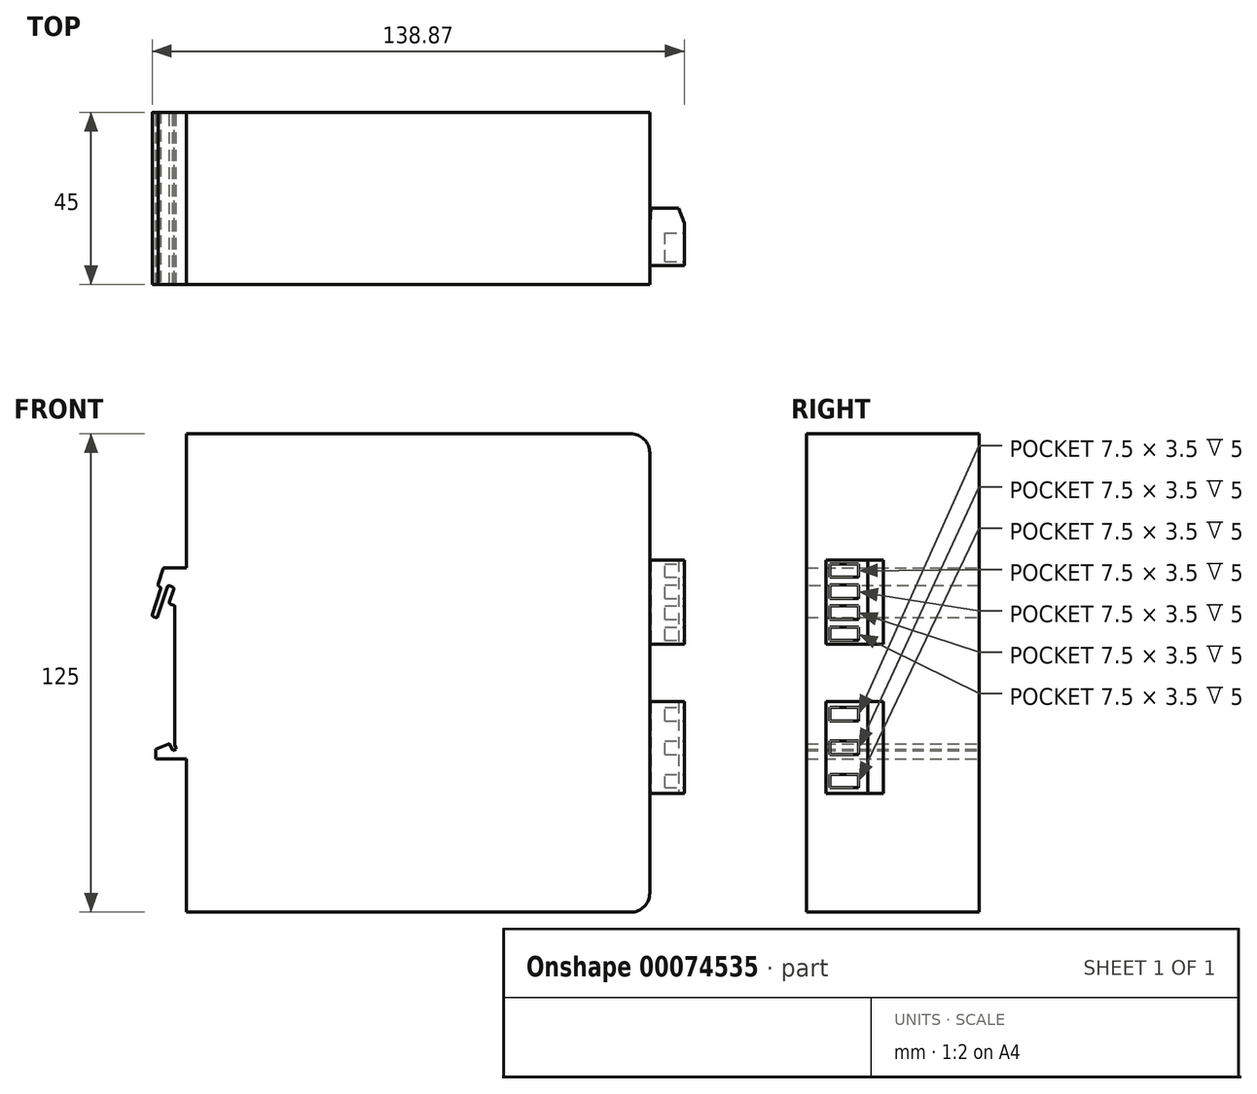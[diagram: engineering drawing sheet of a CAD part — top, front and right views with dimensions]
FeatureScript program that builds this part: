
annotation { "Feature Type Name" : "Feature", "Feature Type Description" : "" }
export const myFeature = defineFeature(function(context is Context, id is Id, definition is map)
    precondition{}
    {
        {
            var Q0;
            Q0=qCreatedBy(makeId("Top.planeOp"),FACE);
            var sketch = newSketch(context, id + "F0", { "sketchPlane" : qUnion([Q0])});
            skLineSegment(sketch, "E0.bottom", {"start": v(-60.5, 22.5) * mm, "end": v(60.5, 22.5) * mm});
            skLineSegment(sketch, "E0.top", {"start": v(-60.5, -22.5) * mm, "end": v(60.5, -22.5) * mm});
            skLineSegment(sketch, "E0.left", {"start": v(-60.5, 22.5) * mm, "end": v(-60.5, -22.5) * mm});
            skLineSegment(sketch, "E0.right", {"start": v(60.5, 22.5) * mm, "end": v(60.5, -22.5) * mm});
            skLineSegment(sketch, "E1", {"start": v(-60.5, 22.5) * mm, "end": v(60.5, -22.5) * mm, "construction": true});
            skLineSegment(sketch, "E2", {"start": v(-60.5, -22.5) * mm, "end": v(60.5, 22.5) * mm, "construction": true});
            skPoint(sketch, "E3", {"position": v(0, 0) * mm});
            skPoint(sketch, "E3.positionSnap0", {"position": v(0, 0) * mm});
            skSolve(sketch);
        }
        {
            var Q0;
            Q0=makeQuery(id+"F0.imprint","IMPRINT",FACE,{"disambiguationData":[TD([[makeQuery(id+"F0.imprint","IMPRINT",EDGE,{"derivedFrom":sQuery(id+"F0.wireOp",EDGE,"E0.bottom")}),-1.0]])]});
            extrude(context, id + "F1", {"entities" : qUnion([Q0]), "depth" : 125 * mm});
        }
        {
            var Q0;
            Q0=makeQuery(id+"F1.opExtrude","CAP_EDGE",EDGE,{"disambiguationData":[OSD([sQuery(id+"F0.wireOp",EDGE,"E0.right")])],"isStart":false});
            var Q1;
            Q1=makeQuery(id+"F1.opExtrude","CAP_EDGE",EDGE,{"disambiguationData":[OSD([sQuery(id+"F0.wireOp",EDGE,"E0.right")])],"isStart":true});
            fillet(context, id + "F2", {"entities" : qUnion([Q0, Q1]), "radius" : 5 * mm, "tangentPropagation" : true, "allowEdgeOverflow" : false});
        }
        {
            var Q0;
            Q0=makeQuery(id+"F1.opExtrude","SWEPT_FACE",FACE,{"disambiguationData":[OSD([sQuery(id+"F0.wireOp",EDGE,"E0.right")])]});
            var sketch = newSketch(context, id + "F3", { "sketchPlane" : qUnion([Q0])});
            skLineSegment(sketch, "E4.bottom", {"start": v(-17.5, 92) * mm, "end": v(-6.5, 92) * mm});
            skLineSegment(sketch, "E4.top", {"start": v(-17.5, 70) * mm, "end": v(-6.5, 70) * mm});
            skLineSegment(sketch, "E4.left", {"start": v(-17.5, 92) * mm, "end": v(-17.5, 70) * mm});
            skLineSegment(sketch, "E4.right", {"start": v(-6.5, 92) * mm, "end": v(-6.5, 70) * mm});
            skLineSegment(sketch, "E5.bottom", {"start": v(-17.5, 55) * mm, "end": v(-6.5, 55) * mm});
            skLineSegment(sketch, "E5.top", {"start": v(-17.5, 31) * mm, "end": v(-6.5, 31) * mm});
            skLineSegment(sketch, "E5.left", {"start": v(-17.5, 55) * mm, "end": v(-17.5, 31) * mm});
            skLineSegment(sketch, "E5.right", {"start": v(-6.5, 55) * mm, "end": v(-6.5, 31) * mm});
            skSolve(sketch);
        }
        {
            var Q0;
            Q0=makeQuery(id+"F3.imprint","IMPRINT",FACE,{"disambiguationData":[TD([[makeQuery(id+"F3.imprint","IMPRINT",EDGE,{"derivedFrom":sQuery(id+"F3.wireOp",EDGE,"E4.bottom")}),-1.0]])]});
            var Q1;
            Q1=makeQuery(id+"F3.imprint","IMPRINT",FACE,{"disambiguationData":[TD([[makeQuery(id+"F3.imprint","IMPRINT",EDGE,{"derivedFrom":sQuery(id+"F3.wireOp",EDGE,"E5.bottom")}),-1.0]])]});
            extrude(context, id + "F4", {"entities" : qUnion([Q0, Q1]), "depth" : 9 * mm});
        }
        {
            var Q0;
            Q0=makeQuery(id+"F4.opExtrude","SWEPT_FACE",FACE,{"disambiguationData":[OSD([sQuery(id+"F3.wireOp",EDGE,"E4.top")])]});
            var sketch = newSketch(context, id + "F5", { "sketchPlane" : qUnion([Q0])});
            skLineSegment(sketch, "E6", {"start": v(69.5, 6.5) * mm, "end": v(68.04, 2.5) * mm});
            skLineSegment(sketch, "E7", {"start": v(68.04, 2.5) * mm, "end": v(60.85, 2.5) * mm});
            skLineSegment(sketch, "E8", {"start": v(60.85, 2.5) * mm, "end": v(60.5, 6.5) * mm});
            skLineSegment(sketch, "E9", {"start": v(60.5, 6.5) * mm, "end": v(69.5, 6.5) * mm});
            skLineSegment(sketch, "E10", {"start": v(68.39, 3.44) * mm, "end": v(68.04, 2.5) * mm});
            skLineSegment(sketch, "E11", {"start": v(68.04, 2.5) * mm, "end": v(69.04, 2.5) * mm});
            skLineSegment(sketch, "E12", {"start": v(69.04, 2.5) * mm, "end": v(68.39, 3.44) * mm});
            skSolve(sketch);
        }
        {
            var Q0;
            Q0=makeQuery(id+"F5.imprint","IMPRINT",FACE,{"disambiguationData":[TD([[makeQuery(id+"F5.imprint","IMPRINT",EDGE,{"derivedFrom":sQuery(id+"F5.wireOp",EDGE,"E6")}),-1.0]])]});
            var Q1;
            Q1=makeQuery(id+"F5.imprint","IMPRINT",FACE,{"disambiguationData":[TD([[makeQuery(id+"F5.imprint","IMPRINT",EDGE,{"derivedFrom":sQuery(id+"F5.wireOp",EDGE,"E10")}),1.0]])]});
            var Q2;
            Q2=makeQuery(id+"F4.opExtrude","SWEPT_FACE",FACE,{"disambiguationData":[OSD([sQuery(id+"F3.wireOp",EDGE,"E4.bottom")])]});
            extrude(context, id + "F6", {"entities" : qUnion([Q0, Q1]), "operationType" : NewBodyOperationType.ADD, "endBound" : BoundingType.UP_TO_SURFACE, "oppositeDirection" : true, "endBoundEntityFace" : qUnion([Q2]), "depth" : 25 * mm});
        }
        {
            var Q0;
            Q0=makeQuery(id+"F4.opExtrude","SWEPT_FACE",FACE,{"disambiguationData":[OSD([sQuery(id+"F3.wireOp",EDGE,"E5.top")])]});
            var sketch = newSketch(context, id + "F7", { "sketchPlane" : qUnion([Q0])});
            skLineSegment(sketch, "E13", {"start": v(69.5, 6.5) * mm, "end": v(68.04, 2.5) * mm});
            skLineSegment(sketch, "E14", {"start": v(68.04, 2.5) * mm, "end": v(60.85, 2.5) * mm});
            skLineSegment(sketch, "E15", {"start": v(60.85, 2.5) * mm, "end": v(60.5, 6.5) * mm});
            skLineSegment(sketch, "E16", {"start": v(60.5, 6.5) * mm, "end": v(69.5, 6.5) * mm});
            skLineSegment(sketch, "E17", {"start": v(68.39, 3.44) * mm, "end": v(68.04, 2.5) * mm});
            skLineSegment(sketch, "E18", {"start": v(68.04, 2.5) * mm, "end": v(69.04, 2.5) * mm});
            skLineSegment(sketch, "E19", {"start": v(69.04, 2.5) * mm, "end": v(68.39, 3.44) * mm});
            skSolve(sketch);
        }
        {
            var Q0;
            Q0=makeQuery(id+"F7.imprint","IMPRINT",FACE,{"disambiguationData":[TD([[makeQuery(id+"F7.imprint","IMPRINT",EDGE,{"derivedFrom":sQuery(id+"F7.wireOp",EDGE,"E13")}),-1.0]])]});
            var Q1;
            Q1=makeQuery(id+"F7.imprint","IMPRINT",FACE,{"disambiguationData":[TD([[makeQuery(id+"F7.imprint","IMPRINT",EDGE,{"derivedFrom":sQuery(id+"F7.wireOp",EDGE,"E17")}),1.0]])]});
            var Q2;
            Q2=makeQuery(id+"F4.opExtrude","SWEPT_FACE",FACE,{"disambiguationData":[OSD([sQuery(id+"F3.wireOp",EDGE,"E5.bottom")])]});
            extrude(context, id + "F8", {"entities" : qUnion([Q0, Q1]), "operationType" : NewBodyOperationType.ADD, "endBound" : BoundingType.UP_TO_SURFACE, "oppositeDirection" : true, "endBoundEntityFace" : qUnion([Q2]), "depth" : 25 * mm});
        }
        {
            var Q0;
            Q0=makeQuery(id+"F4.opExtrude","CAP_FACE",FACE,{"disambiguationData":[OSD([sQuery(id+"F3.wireOp",EDGE,"E5.bottom"),sQuery(id+"F3.wireOp",EDGE,"E5.top"),sQuery(id+"F3.wireOp",EDGE,"E5.left"),sQuery(id+"F3.wireOp",EDGE,"E5.right")])],"isStart":false});
            var sketch = newSketch(context, id + "F9", { "sketchPlane" : qUnion([Q0])});
            skLineSegment(sketch, "E20.bottom", {"start": v(-16.5, 32.5) * mm, "end": v(-9, 32.5) * mm});
            skLineSegment(sketch, "E20.top", {"start": v(-16.5, 36) * mm, "end": v(-9, 36) * mm});
            skLineSegment(sketch, "E20.left", {"start": v(-16.5, 32.5) * mm, "end": v(-16.5, 36) * mm});
            skLineSegment(sketch, "E20.right", {"start": v(-9, 32.5) * mm, "end": v(-9, 36) * mm});
            skLineSegment(sketch, "E21.bottom", {"start": v(-16.5, 41.25) * mm, "end": v(-9, 41.25) * mm});
            skLineSegment(sketch, "E21.top", {"start": v(-16.5, 44.75) * mm, "end": v(-9, 44.75) * mm});
            skLineSegment(sketch, "E21.left", {"start": v(-16.5, 41.25) * mm, "end": v(-16.5, 44.75) * mm});
            skLineSegment(sketch, "E21.right", {"start": v(-9, 41.25) * mm, "end": v(-9, 44.75) * mm});
            skLineSegment(sketch, "E22.bottom", {"start": v(-16.5, 50) * mm, "end": v(-9, 50) * mm});
            skLineSegment(sketch, "E22.top", {"start": v(-16.5, 53.5) * mm, "end": v(-9, 53.5) * mm});
            skLineSegment(sketch, "E22.left", {"start": v(-16.5, 50) * mm, "end": v(-16.5, 53.5) * mm});
            skLineSegment(sketch, "E22.right", {"start": v(-9, 50) * mm, "end": v(-9, 53.5) * mm});
            skLineSegment(sketch, "E23.bottom", {"start": v(-16.5, 71) * mm, "end": v(-9, 71) * mm});
            skLineSegment(sketch, "E23.top", {"start": v(-16.5, 74.5) * mm, "end": v(-9, 74.5) * mm});
            skLineSegment(sketch, "E23.left", {"start": v(-16.5, 71) * mm, "end": v(-16.5, 74.5) * mm});
            skLineSegment(sketch, "E23.right", {"start": v(-9, 71) * mm, "end": v(-9, 74.5) * mm});
            skLineSegment(sketch, "E24.bottom", {"start": v(-16.5, 76.5) * mm, "end": v(-9, 76.5) * mm});
            skLineSegment(sketch, "E24.top", {"start": v(-16.5, 80) * mm, "end": v(-9, 80) * mm});
            skLineSegment(sketch, "E24.left", {"start": v(-16.5, 76.5) * mm, "end": v(-16.5, 80) * mm});
            skLineSegment(sketch, "E24.right", {"start": v(-9, 76.5) * mm, "end": v(-9, 80) * mm});
            skLineSegment(sketch, "E25.bottom", {"start": v(-16.5, 82) * mm, "end": v(-9, 82) * mm});
            skLineSegment(sketch, "E25.top", {"start": v(-16.5, 85.5) * mm, "end": v(-9, 85.5) * mm});
            skLineSegment(sketch, "E25.left", {"start": v(-16.5, 82) * mm, "end": v(-16.5, 85.5) * mm});
            skLineSegment(sketch, "E25.right", {"start": v(-9, 82) * mm, "end": v(-9, 85.5) * mm});
            skLineSegment(sketch, "E26.bottom", {"start": v(-16.5, 87.5) * mm, "end": v(-9, 87.5) * mm});
            skLineSegment(sketch, "E26.top", {"start": v(-16.5, 91) * mm, "end": v(-9, 91) * mm});
            skLineSegment(sketch, "E26.left", {"start": v(-16.5, 87.5) * mm, "end": v(-16.5, 91) * mm});
            skLineSegment(sketch, "E26.right", {"start": v(-9, 87.5) * mm, "end": v(-9, 91) * mm});
            skSolve(sketch);
        }
        {
            var Q0;
            Q0=makeQuery(id+"F9.imprint","IMPRINT",FACE,{"disambiguationData":[TD([[makeQuery(id+"F9.imprint","IMPRINT",EDGE,{"derivedFrom":sQuery(id+"F9.wireOp",EDGE,"E20.bottom")}),1.0]])]});
            var Q1;
            Q1=makeQuery(id+"F9.imprint","IMPRINT",FACE,{"disambiguationData":[TD([[makeQuery(id+"F9.imprint","IMPRINT",EDGE,{"derivedFrom":sQuery(id+"F9.wireOp",EDGE,"tqbWb7Cq-eTrh-Zdbz-2FrB-U6ubUCRYbAbA.bottom")}),1.0]])]});
            var Q2;
            Q2=makeQuery(id+"F9.imprint","IMPRINT",FACE,{"disambiguationData":[TD([[makeQuery(id+"F9.imprint","IMPRINT",EDGE,{"derivedFrom":sQuery(id+"F9.wireOp",EDGE,"E21.bottom")}),1.0]])]});
            var Q3;
            Q3=makeQuery(id+"F9.imprint","IMPRINT",FACE,{"disambiguationData":[TD([[makeQuery(id+"F9.imprint","IMPRINT",EDGE,{"derivedFrom":sQuery(id+"F9.wireOp",EDGE,"E22.bottom")}),1.0]])]});
            extrude(context, id + "F10", {"entities" : qUnion([Q0, Q1, Q2, Q3]), "operationType" : NewBodyOperationType.REMOVE, "oppositeDirection" : true, "depth" : 5 * mm});
        }
        {
            var Q0;
            Q0=makeQuery(id+"F9.imprint","IMPRINT",FACE,{"disambiguationData":[TD([[makeQuery(id+"F9.imprint","IMPRINT",EDGE,{"derivedFrom":sQuery(id+"F9.wireOp",EDGE,"E23.bottom")}),1.0]])]});
            var Q1;
            Q1=makeQuery(id+"F9.imprint","IMPRINT",FACE,{"disambiguationData":[TD([[makeQuery(id+"F9.imprint","IMPRINT",EDGE,{"derivedFrom":sQuery(id+"F9.wireOp",EDGE,"E24.bottom")}),1.0]])]});
            var Q2;
            Q2=makeQuery(id+"F9.imprint","IMPRINT",FACE,{"disambiguationData":[TD([[makeQuery(id+"F9.imprint","IMPRINT",EDGE,{"derivedFrom":sQuery(id+"F9.wireOp",EDGE,"E25.bottom")}),1.0]])]});
            var Q3;
            Q3=makeQuery(id+"F9.imprint","IMPRINT",FACE,{"disambiguationData":[TD([[makeQuery(id+"F9.imprint","IMPRINT",EDGE,{"derivedFrom":sQuery(id+"F9.wireOp",EDGE,"E26.bottom")}),1.0]])]});
            extrude(context, id + "F11", {"entities" : qUnion([Q0, Q1, Q2, Q3]), "operationType" : NewBodyOperationType.REMOVE, "oppositeDirection" : true, "depth" : 5 * mm});
        }
        {
            var Q0;
            Q0=makeQuery(id+"F1.opExtrude","SWEPT_FACE",FACE,{"disambiguationData":[OSD([sQuery(id+"F0.wireOp",EDGE,"E0.bottom")])]});
            var sketch = newSketch(context, id + "F12", { "sketchPlane" : qUnion([Q0])});
            skLineSegment(sketch, "E27", {"start": v(60.5, 40) * mm, "end": v(60.5, 90) * mm});
            skLineSegment(sketch, "E28", {"start": v(60.5, 90) * mm, "end": v(66.5, 90) * mm});
            skLineSegment(sketch, "E29", {"start": v(66.5, 90) * mm, "end": v(68.02, 85.24) * mm});
            skLineSegment(sketch, "E30", {"start": v(68.02, 85.24) * mm, "end": v(67.07, 84.93) * mm});
            skLineSegment(sketch, "E31", {"start": v(67.07, 84.93) * mm, "end": v(69.5, 77.31) * mm});
            skLineSegment(sketch, "E32", {"start": v(69.5, 77.31) * mm, "end": v(68.07, 76.86) * mm});
            skLineSegment(sketch, "E33", {"start": v(68.07, 76.86) * mm, "end": v(65.33, 85.43) * mm});
            skLineSegment(sketch, "E34", {"start": v(65.33, 85.43) * mm, "end": v(63.68, 84.9) * mm});
            skLineSegment(sketch, "E35", {"start": v(63.68, 84.9) * mm, "end": v(65.04, 80.61) * mm});
            skLineSegment(sketch, "E36", {"start": v(65.04, 80.61) * mm, "end": v(63.5, 80.12) * mm});
            skLineSegment(sketch, "E37", {"start": v(63.5, 80.12) * mm, "end": v(63.5, 43.55) * mm});
            skLineSegment(sketch, "E38", {"start": v(63.5, 43.55) * mm, "end": v(63.12, 42.62) * mm});
            skLineSegment(sketch, "E39", {"start": v(63.12, 42.62) * mm, "end": v(64.04, 42.24) * mm});
            skLineSegment(sketch, "E40", {"start": v(64.04, 42.24) * mm, "end": v(64.8, 44.09) * mm});
            skLineSegment(sketch, "E41", {"start": v(64.8, 44.09) * mm, "end": v(68.5, 42.55) * mm});
            skLineSegment(sketch, "E42", {"start": v(68.5, 42.55) * mm, "end": v(68.5, 40.05) * mm});
            skLineSegment(sketch, "E43", {"start": v(68.5, 40.05) * mm, "end": v(60.5, 40) * mm});
            skSolve(sketch);
        }
        {
            var Q0;
            Q0=makeQuery(id+"F12.imprint","IMPRINT",FACE,{"disambiguationData":[TD([[makeQuery(id+"F12.imprint","IMPRINT",EDGE,{"derivedFrom":sQuery(id+"F12.wireOp",EDGE,"E27")}),1.0]])]});
            var Q1;
            Q1=makeQuery(id+"F1.opExtrude","SWEPT_FACE",FACE,{"disambiguationData":[OSD([sQuery(id+"F0.wireOp",EDGE,"E0.top")])]});
            extrude(context, id + "F13", {"entities" : qUnion([Q0]), "operationType" : NewBodyOperationType.ADD, "endBound" : BoundingType.UP_TO_SURFACE, "oppositeDirection" : true, "endBoundEntityFace" : qUnion([Q1]), "depth" : 25 * mm});
        }
        {
            var Q0;
            Q0=makeQuery(id+"F13.opExtrude","SWEPT_EDGE",EDGE,{"disambiguationData":[OSD([sQuery(id+"F12.wireOp",EDGE,"E30"),sQuery(id+"F12.wireOp",EDGE,"E31")])]});
            var Q1;
            Q1=makeQuery(id+"F13.opExtrude","SWEPT_EDGE",EDGE,{"disambiguationData":[OSD([sQuery(id+"F12.wireOp",EDGE,"E34"),sQuery(id+"F12.wireOp",EDGE,"E35")])]});
            var Q2;
            Q2=makeQuery(id+"F13.opExtrude","SWEPT_EDGE",EDGE,{"disambiguationData":[OSD([sQuery(id+"F12.wireOp",EDGE,"E36"),sQuery(id+"F12.wireOp",EDGE,"E37")])]});
            fillet(context, id + "F14", {"entities" : qUnion([Q0, Q1, Q2]), "radius" : 0.5 * mm, "tangentPropagation" : true, "allowEdgeOverflow" : false});
        }
        {
            var Q0;
            Q0=makeQuery(id+"F13.opExtrude","SWEPT_EDGE",EDGE,{"disambiguationData":[OSD([sQuery(id+"F12.wireOp",EDGE,"E29"),sQuery(id+"F12.wireOp",EDGE,"E30")])]});
            var Q1;
            Q1=makeQuery(id+"F13.opExtrude","SWEPT_EDGE",EDGE,{"disambiguationData":[OSD([sQuery(id+"F12.wireOp",EDGE,"E31"),sQuery(id+"F12.wireOp",EDGE,"E32")])]});
            var Q2;
            Q2=makeQuery(id+"F13.opExtrude","SWEPT_EDGE",EDGE,{"disambiguationData":[OSD([sQuery(id+"F12.wireOp",EDGE,"E32"),sQuery(id+"F12.wireOp",EDGE,"E33")])]});
            var Q3;
            Q3=makeQuery(id+"F13.opExtrude","SWEPT_EDGE",EDGE,{"disambiguationData":[OSD([sQuery(id+"F12.wireOp",EDGE,"E33"),sQuery(id+"F12.wireOp",EDGE,"E34")])]});
            var Q4;
            Q4=makeQuery(id+"F13.opExtrude","SWEPT_EDGE",EDGE,{"disambiguationData":[OSD([sQuery(id+"F12.wireOp",EDGE,"E28"),sQuery(id+"F12.wireOp",EDGE,"E29")])]});
            var Q5;
            Q5=makeQuery(id+"F13.opExtrude","SWEPT_EDGE",EDGE,{"disambiguationData":[OSD([sQuery(id+"F12.wireOp",EDGE,"E35"),sQuery(id+"F12.wireOp",EDGE,"E36")])]});
            var Q6;
            Q6=makeQuery(id+"F13.opExtrude","SWEPT_EDGE",EDGE,{"disambiguationData":[OSD([sQuery(id+"F12.wireOp",EDGE,"E40"),sQuery(id+"F12.wireOp",EDGE,"E41")])]});
            var Q7;
            Q7=makeQuery(id+"F13.opExtrude","SWEPT_EDGE",EDGE,{"disambiguationData":[OSD([sQuery(id+"F12.wireOp",EDGE,"E37"),sQuery(id+"F12.wireOp",EDGE,"E38")])]});
            fillet(context, id + "F15", {"entities" : qUnion([Q0, Q1, Q2, Q3, Q4, Q5, Q6, Q7]), "radius" : 0.5 * mm, "tangentPropagation" : true, "allowEdgeOverflow" : false});
        }
    });
